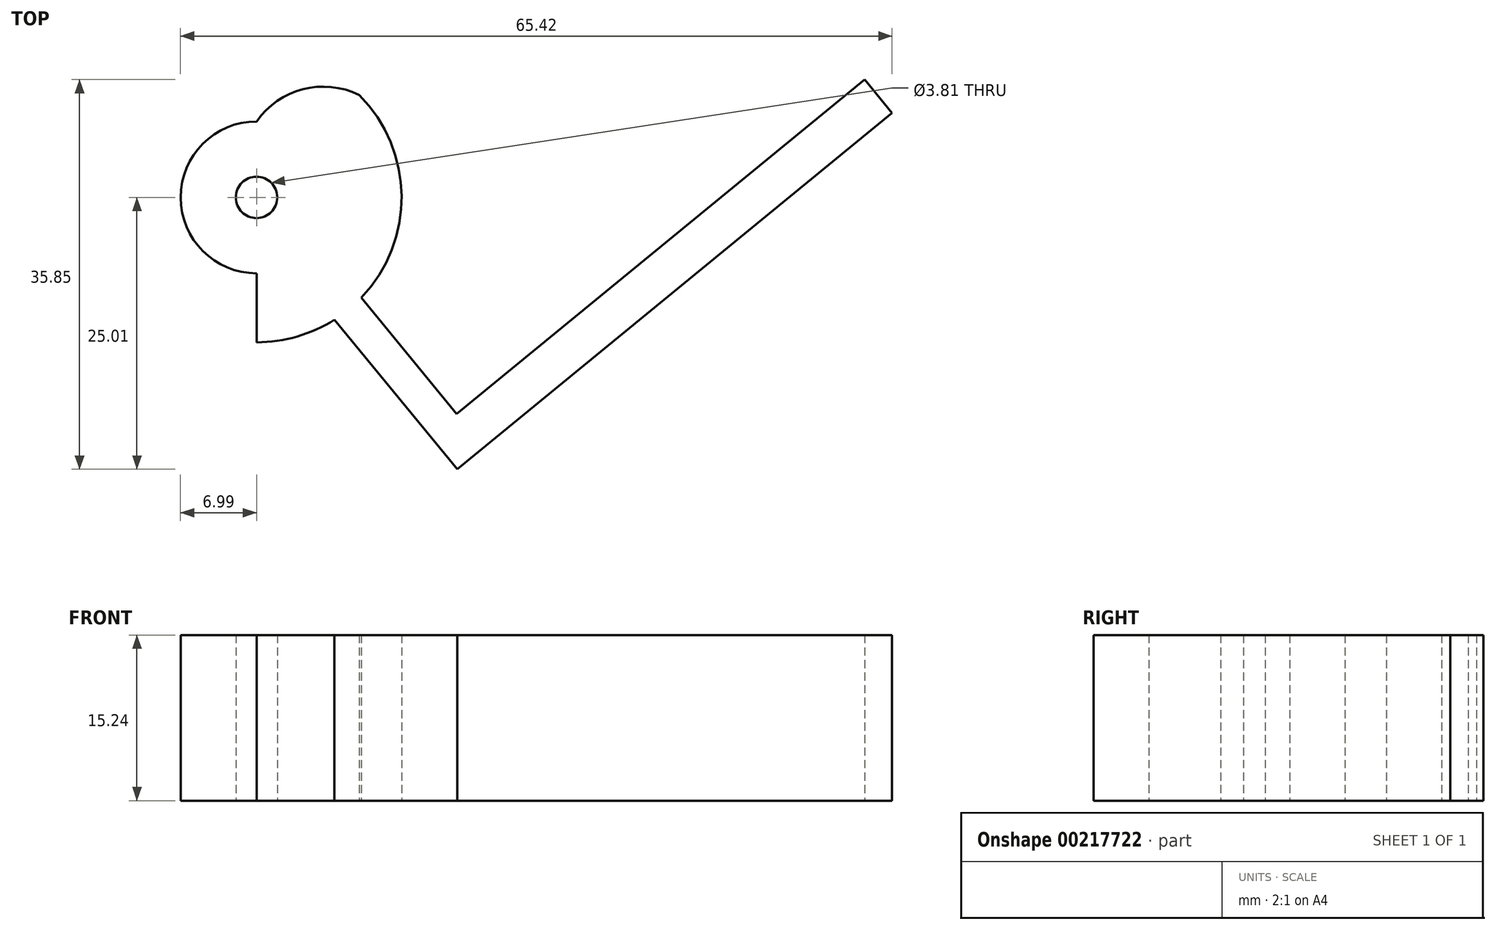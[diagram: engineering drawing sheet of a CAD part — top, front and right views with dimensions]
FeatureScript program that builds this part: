
annotation { "Feature Type Name" : "Feature", "Feature Type Description" : "" }
export const myFeature = defineFeature(function(context is Context, id is Id, definition is map)
    precondition{}
    {
        {
            var Q0;
            Q0=qCreatedBy(makeId("Top.planeOp"),FACE);
            var sketch = newSketch(context, id + "F0", { "sketchPlane" : qUnion([Q0])});
            skCircle(sketch, "E0", {"center": v(0, 0) * mm, "radius": 1.9 * mm});
            skArc(sketch, "E1", {"start": v(0, 6.99) * mm, "mid": v(-6.99, 0) * mm, "end": v(0, -6.99) * mm});
            skArc(sketch, "E2", {"start": v(0, -13.34) * mm, "mid": v(12.32, -5.1) * mm, "end": v(9.43, 9.43) * mm});
            skArc(sketch, "E3", {"start": v(9.43, 9.43) * mm, "mid": v(4.26, 9.95) * mm, "end": v(0, 6.99) * mm});
            skLineSegment(sketch, "E4", {"start": v(0, -6.99) * mm, "end": v(0, -13.34) * mm});
            skLineSegment(sketch, "E5", {"start": v(1.2, -1.47) * mm, "end": v(19.69, -24) * mm});
            skLineSegment(sketch, "E6.0", {"start": v(-0.56, -1.82) * mm, "end": v(18.46, -25) * mm});
            skLineSegment(sketch, "E7.0", {"start": v(1.9, 0.2) * mm, "end": v(20.92, -23) * mm});
            skLineSegment(sketch, "E8", {"start": v(18.4, -19.93) * mm, "end": v(42.7, 0) * mm});
            skLineSegment(sketch, "E9", {"start": v(42.7, 0) * mm, "end": v(45.22, -3.06) * mm});
            skLineSegment(sketch, "E10", {"start": v(45.22, -3.06) * mm, "end": v(20.92, -23) * mm});
            skLineSegment(sketch, "E11", {"start": v(20.92, -23) * mm, "end": v(18.46, -25) * mm});
            skLineSegment(sketch, "E12", {"start": v(42.7, 0) * mm, "end": v(55.92, 10.84) * mm});
            skLineSegment(sketch, "E13", {"start": v(45.22, -3.06) * mm, "end": v(59.96, 9.03) * mm});
            skLineSegment(sketch, "E14", {"start": v(55.92, 10.84) * mm, "end": v(60.64, 5.09) * mm});
            skSolve(sketch);
        }
        {
            var Q0;
            Q0 = qSketchRegion(id + "F0", true);
            extrude(context, id + "F1", {"entities" : qUnion([Q0]), "depth" : 15.24 * mm});
        }
    });
